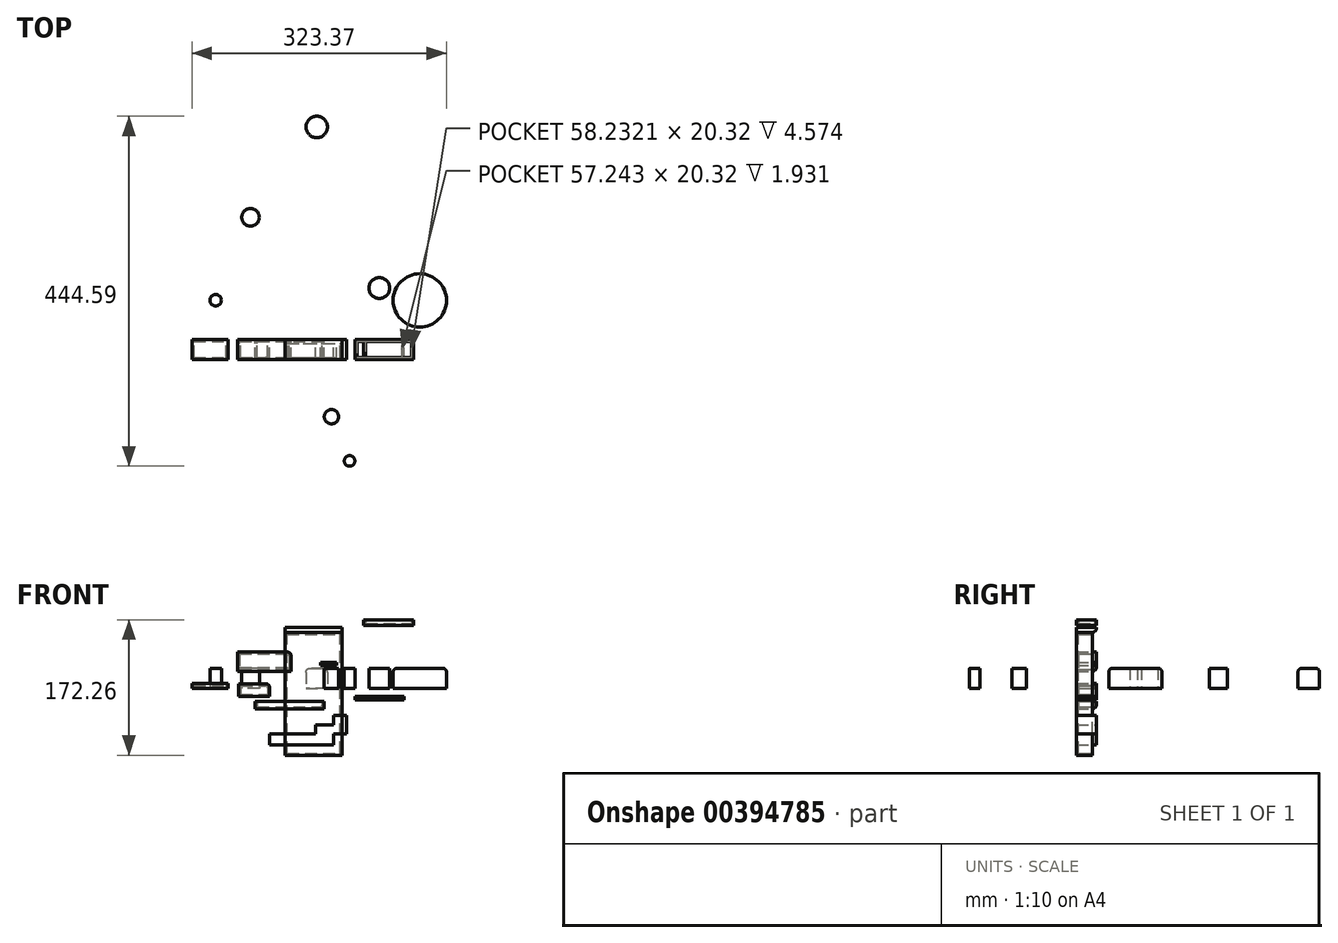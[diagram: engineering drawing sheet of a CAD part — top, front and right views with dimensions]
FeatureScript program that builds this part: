
annotation { "Feature Type Name" : "Feature", "Feature Type Description" : "" }
export const myFeature = defineFeature(function(context is Context, id is Id, definition is map)
    precondition{}
    {
        {
            var Q0;
            Q0=qCreatedBy(makeId("Front.planeOp"),FACE);
            var sketch = newSketch(context, id + "F0", { "sketchPlane" : qUnion([Q0])});
            skLineSegment(sketch, "E0.bottom", {"start": v(-105.2, 46.14) * mm, "end": v(-37.26, 46.14) * mm});
            skLineSegment(sketch, "E0.top", {"start": v(-105.2, 21.56) * mm, "end": v(-37.26, 21.56) * mm});
            skLineSegment(sketch, "E0.left", {"start": v(-105.2, 46.14) * mm, "end": v(-105.2, 21.56) * mm});
            skLineSegment(sketch, "E0.right", {"start": v(-37.26, 46.14) * mm, "end": v(-37.26, 21.56) * mm});
            skLineSegment(sketch, "E1.bottom", {"start": v(-163.23, 6.3) * mm, "end": v(-117.4, 6.3) * mm});
            skLineSegment(sketch, "E1.top", {"start": v(-163.23, 0) * mm, "end": v(-117.4, 0) * mm});
            skLineSegment(sketch, "E1.left", {"start": v(-163.23, 6.3) * mm, "end": v(-163.23, 0) * mm});
            skLineSegment(sketch, "E1.right", {"start": v(-117.4, 6.3) * mm, "end": v(-117.4, 0) * mm});
            skLineSegment(sketch, "E2.bottom", {"start": v(-103.87, 5.63) * mm, "end": v(-64.3, 5.63) * mm});
            skLineSegment(sketch, "E2.top", {"start": v(-103.87, -10.65) * mm, "end": v(-64.3, -10.65) * mm});
            skLineSegment(sketch, "E2.left", {"start": v(-103.87, 5.63) * mm, "end": v(-103.87, -10.65) * mm});
            skLineSegment(sketch, "E2.right", {"start": v(-64.3, 5.63) * mm, "end": v(-64.3, -10.65) * mm});
            skLineSegment(sketch, "E3.bottom", {"start": v(-82.77, -16.97) * mm, "end": v(4.62, -16.97) * mm});
            skLineSegment(sketch, "E3.top", {"start": v(-82.77, -26.04) * mm, "end": v(4.62, -26.04) * mm});
            skLineSegment(sketch, "E3.left", {"start": v(-82.77, -16.97) * mm, "end": v(-82.77, -26.04) * mm});
            skLineSegment(sketch, "E3.right", {"start": v(4.62, -16.97) * mm, "end": v(4.62, -26.04) * mm});
            skLineSegment(sketch, "E4.bottom", {"start": v(0, 32.88) * mm, "end": v(20.77, 32.88) * mm});
            skLineSegment(sketch, "E4.top", {"start": v(0, 29.08) * mm, "end": v(20.77, 29.08) * mm});
            skLineSegment(sketch, "E4.left", {"start": v(0, 32.88) * mm, "end": v(0, 29.08) * mm});
            skLineSegment(sketch, "E4.right", {"start": v(20.77, 32.88) * mm, "end": v(20.77, 29.08) * mm});
            skLineSegment(sketch, "E5.bottom", {"start": v(-44.85, 77.4) * mm, "end": v(27.7, 77.4) * mm});
            skLineSegment(sketch, "E5.top", {"start": v(-44.85, 70.98) * mm, "end": v(27.7, 70.98) * mm});
            skLineSegment(sketch, "E5.left", {"start": v(-44.85, 77.4) * mm, "end": v(-44.85, 70.98) * mm});
            skLineSegment(sketch, "E5.right", {"start": v(27.7, 77.4) * mm, "end": v(27.7, 70.98) * mm});
            skLineSegment(sketch, "E6.bottom", {"start": v(54.74, 87.03) * mm, "end": v(118.05, 87.03) * mm});
            skLineSegment(sketch, "E6.top", {"start": v(54.74, 79.91) * mm, "end": v(118.05, 79.91) * mm});
            skLineSegment(sketch, "E6.left", {"start": v(54.74, 87.03) * mm, "end": v(54.74, 79.91) * mm});
            skLineSegment(sketch, "E6.right", {"start": v(118.05, 87.03) * mm, "end": v(118.05, 79.91) * mm});
            skLineSegment(sketch, "E7.bottom", {"start": v(16.82, -34.39) * mm, "end": v(33.3, -34.39) * mm});
            skLineSegment(sketch, "E7.top", {"start": v(16.82, -57.98) * mm, "end": v(33.3, -57.98) * mm});
            skLineSegment(sketch, "E7.left", {"start": v(16.82, -34.39) * mm, "end": v(16.82, -57.98) * mm});
            skLineSegment(sketch, "E7.right", {"start": v(33.3, -34.39) * mm, "end": v(33.3, -57.98) * mm});
            skLineSegment(sketch, "E8.bottom", {"start": v(-5.94, -46.89) * mm, "end": v(16.82, -46.89) * mm});
            skLineSegment(sketch, "E8.top", {"start": v(-5.94, -57.98) * mm, "end": v(16.82, -57.98) * mm});
            skLineSegment(sketch, "E8.left", {"start": v(-5.94, -46.89) * mm, "end": v(-5.94, -57.98) * mm});
            skLineSegment(sketch, "E8.right", {"start": v(16.82, -46.89) * mm, "end": v(16.82, -57.98) * mm});
            skLineSegment(sketch, "E9.bottom", {"start": v(-64.3, -57.98) * mm, "end": v(16.82, -57.98) * mm});
            skLineSegment(sketch, "E9.top", {"start": v(-64.3, -71.98) * mm, "end": v(16.82, -71.98) * mm});
            skLineSegment(sketch, "E9.left", {"start": v(-64.3, -57.98) * mm, "end": v(-64.3, -71.98) * mm});
            skLineSegment(sketch, "E9.right", {"start": v(16.82, -57.98) * mm, "end": v(16.82, -71.98) * mm});
            skLineSegment(sketch, "E10.bottom", {"start": v(67.6, -72.82) * mm, "end": v(28.36, -72.82) * mm});
            skLineSegment(sketch, "E10.top", {"start": v(67.6, -57.98) * mm, "end": v(28.36, -57.98) * mm});
            skLineSegment(sketch, "E10.left", {"start": v(67.6, -72.82) * mm, "end": v(67.6, -57.98) * mm});
            skLineSegment(sketch, "E10.right", {"start": v(28.36, -72.82) * mm, "end": v(28.36, -57.98) * mm});
            skLineSegment(sketch, "E11.bottom", {"start": v(28.36, -82.82) * mm, "end": v(16.82, -82.82) * mm});
            skLineSegment(sketch, "E11.top", {"start": v(28.36, -57.98) * mm, "end": v(16.82, -57.98) * mm});
            skLineSegment(sketch, "E11.left", {"start": v(28.36, -82.82) * mm, "end": v(28.36, -57.98) * mm});
            skLineSegment(sketch, "E11.right", {"start": v(16.82, -82.82) * mm, "end": v(16.82, -57.98) * mm});
            skLineSegment(sketch, "E12.bottom", {"start": v(28.36, -82.82) * mm, "end": v(67.6, -82.82) * mm});
            skLineSegment(sketch, "E12.top", {"start": v(28.36, -72.82) * mm, "end": v(67.6, -72.82) * mm});
            skLineSegment(sketch, "E12.left", {"start": v(28.36, -82.82) * mm, "end": v(28.36, -72.82) * mm});
            skLineSegment(sketch, "E12.right", {"start": v(67.6, -82.82) * mm, "end": v(67.6, -72.82) * mm});
            skLineSegment(sketch, "E13.bottom", {"start": v(44.19, -14.94) * mm, "end": v(106.5, -14.94) * mm});
            skLineSegment(sketch, "E13.top", {"start": v(44.19, -10.47) * mm, "end": v(106.5, -10.47) * mm});
            skLineSegment(sketch, "E13.left", {"start": v(44.19, -14.94) * mm, "end": v(44.19, -10.47) * mm});
            skLineSegment(sketch, "E13.right", {"start": v(106.5, -14.94) * mm, "end": v(106.5, -10.47) * mm});
            skSolve(sketch);
        }
        {
            var Q0;
            Q0=makeQuery(id+"F0.imprint","IMPRINT",FACE,{"disambiguationData":[TD([[makeQuery(id+"F0.imprint","IMPRINT",EDGE,{"derivedFrom":sQuery(id+"F0.wireOp",EDGE,"E0.bottom")}),-1.0]])]});
            var Q1;
            Q1=makeQuery(id+"F0.imprint","IMPRINT",FACE,{"disambiguationData":[TD([[makeQuery(id+"F0.imprint","IMPRINT",EDGE,{"derivedFrom":sQuery(id+"F0.wireOp",EDGE,"E2.bottom")}),-1.0]])]});
            var Q2;
            Q2=makeQuery(id+"F0.imprint","IMPRINT",FACE,{"disambiguationData":[TD([[makeQuery(id+"F0.imprint","IMPRINT",EDGE,{"derivedFrom":sQuery(id+"F0.wireOp",EDGE,"E1.bottom")}),-1.0]])]});
            var Q3;
            Q3=makeQuery(id+"F0.imprint","IMPRINT",FACE,{"disambiguationData":[TD([[makeQuery(id+"F0.imprint","IMPRINT",EDGE,{"derivedFrom":sQuery(id+"F0.wireOp",EDGE,"E3.bottom")}),-1.0]])]});
            var Q4;
            Q4=makeQuery(id+"F0.imprint","IMPRINT",FACE,{"disambiguationData":[TD([[makeQuery(id+"F0.imprint","IMPRINT",EDGE,{"derivedFrom":sQuery(id+"F0.wireOp",EDGE,"E5.bottom")}),-1.0]])]});
            var Q5;
            Q5=makeQuery(id+"F0.imprint","IMPRINT",FACE,{"disambiguationData":[TD([[makeQuery(id+"F0.imprint","IMPRINT",EDGE,{"derivedFrom":sQuery(id+"F0.wireOp",EDGE,"E4.bottom")}),-1.0]])]});
            var Q6;
            Q6=makeQuery(id+"F0.imprint","IMPRINT",FACE,{"disambiguationData":[TD([[makeQuery(id+"F0.imprint","IMPRINT",EDGE,{"derivedFrom":sQuery(id+"F0.wireOp",EDGE,"E6.bottom")}),-1.0]])]});
            var Q7;
            Q7=makeQuery(id+"F0.imprint","IMPRINT",FACE,{"disambiguationData":[TD([[makeQuery(id+"F0.imprint","IMPRINT",EDGE,{"derivedFrom":sQuery(id+"F0.wireOp",EDGE,"E13.bottom")}),1.0]])]});
            var Q8;
            Q8=makeQuery(id+"F0.imprint","IMPRINT",FACE,{"disambiguationData":[TD([[makeQuery(id+"F0.imprint","IMPRINT",EDGE,{"derivedFrom":sQuery(id+"F0.wireOp",EDGE,"E7.bottom")}),-1.0]])]});
            var Q9;
            Q9=makeQuery(id+"F0.imprint","IMPRINT",FACE,{"disambiguationData":[TD([[makeQuery(id+"F0.imprint","IMPRINT",EDGE,{"derivedFrom":sQuery(id+"F0.wireOp",EDGE,"E8.bottom")}),-1.0]])]});
            var Q10;
            {var subQ1=sQuery(id+"F0.wireOp",EDGE,"E9.top");Q10=makeQuery(id+"F0.imprint","IMPRINT",FACE,{"disambiguationData":[TD([[makeQuery(id+"F0.imprint","IMPRINT",EDGE,{"derivedFrom":subQ1}),1.0]])]});}
            extrude(context, id + "F1", {"entities" : qUnion([Q0, Q1, Q2, Q3, Q4, Q5, Q6, Q7, Q8, Q9, Q10]), "depth" : 25.4 * mm});
        }
        {
            var Q0;
            Q0=makeQuery(id+"F1.opExtrude","SWEPT_EDGE",EDGE,{"disambiguationData":[OSD([sQuery(id+"F0.wireOp",EDGE,"E7.bottom"),sQuery(id+"F0.wireOp",EDGE,"E7.right")])]});
            var Q1;
            Q1=makeQuery(id+"F1.opExtrude","SWEPT_EDGE",EDGE,{"disambiguationData":[OSD([sQuery(id+"F0.wireOp",EDGE,"E0.bottom"),sQuery(id+"F0.wireOp",EDGE,"E0.right")])]});
            var Q2;
            Q2=makeQuery(id+"F1.opExtrude","SWEPT_EDGE",EDGE,{"disambiguationData":[OSD([sQuery(id+"F0.wireOp",EDGE,"E2.bottom"),sQuery(id+"F0.wireOp",EDGE,"E2.right")])]});
            var Q3;
            Q3=makeQuery(id+"F1.opExtrude","SWEPT_EDGE",EDGE,{"disambiguationData":[OSD([sQuery(id+"F0.wireOp",EDGE,"E7.right"),sQuery(id+"F0.wireOp",EDGE,"E10.top")])]});
            var Q4;
            Q4=makeQuery(id+"F1.opExtrude","CAP_EDGE",EDGE,{"disambiguationData":[OSD([sQuery(id+"F0.wireOp",EDGE,"E7.bottom")])],"isStart":false});
            var Q5;
            Q5=makeQuery(id+"F1.opExtrude","SWEPT_EDGE",EDGE,{"disambiguationData":[OSD([sQuery(id+"F0.wireOp",EDGE,"E7.left"),sQuery(id+"F0.wireOp",EDGE,"E8.bottom"),sQuery(id+"F0.wireOp",EDGE,"E8.right")])]});
            var Q6;
            Q6=makeQuery(id+"F1.opExtrude","SWEPT_EDGE",EDGE,{"disambiguationData":[OSD([sQuery(id+"F0.wireOp",EDGE,"E8.bottom"),sQuery(id+"F0.wireOp",EDGE,"E8.left")])]});
            var Q7;
            Q7=makeQuery(id+"F1.opExtrude","SWEPT_EDGE",EDGE,{"disambiguationData":[OSD([sQuery(id+"F0.wireOp",EDGE,"E8.left"),sQuery(id+"F0.wireOp",EDGE,"E9.bottom")])]});
            var Q8;
            Q8=makeQuery(id+"F1.opExtrude","SWEPT_EDGE",EDGE,{"disambiguationData":[OSD([sQuery(id+"F0.wireOp",EDGE,"E7.bottom"),sQuery(id+"F0.wireOp",EDGE,"E7.left")])]});
            var Q9;
            Q9=makeQuery(id+"F1.opExtrude","SWEPT_EDGE",EDGE,{"disambiguationData":[OSD([sQuery(id+"F0.wireOp",EDGE,"E9.bottom"),sQuery(id+"F0.wireOp",EDGE,"E9.left")])]});
            var Q10;
            Q10=makeQuery(id+"F1.opExtrude","SWEPT_EDGE",EDGE,{"disambiguationData":[OSD([sQuery(id+"F0.wireOp",EDGE,"E8.right"),sQuery(id+"F0.wireOp",EDGE,"E9.bottom"),sQuery(id+"F0.wireOp",EDGE,"E11.top"),sQuery(id+"F0.wireOp",EDGE,"E11.right")])]});
            var Q11;
            Q11=makeQuery(id+"F1.opExtrude","SWEPT_FACE",FACE,{"disambiguationData":[OSD([sQuery(id+"F0.wireOp",EDGE,"E9.top")])]});
            var Q12;
            Q12=makeQuery(id+"F1.opExtrude","CAP_EDGE",EDGE,{"disambiguationData":[OSD([sQuery(id+"F0.wireOp",EDGE,"E9.bottom")])],"isStart":true});
            var Q13;
            Q13=makeQuery(id+"F1.opExtrude","CAP_EDGE",EDGE,{"disambiguationData":[OSD([sQuery(id+"F0.wireOp",EDGE,"E10.top"),sQuery(id+"F0.wireOp",EDGE,"E11.top")])],"isStart":true});
            var Q14;
            Q14=makeQuery(id+"F1.opExtrude","CAP_EDGE",EDGE,{"disambiguationData":[OSD([sQuery(id+"F0.wireOp",EDGE,"E7.right")])],"isStart":true});
            var Q15;
            Q15=makeQuery(id+"F1.opExtrude","CAP_EDGE",EDGE,{"disambiguationData":[OSD([sQuery(id+"F0.wireOp",EDGE,"E7.bottom")])],"isStart":true});
            var Q16;
            Q16=makeQuery(id+"F1.opExtrude","CAP_EDGE",EDGE,{"disambiguationData":[OSD([sQuery(id+"F0.wireOp",EDGE,"E8.bottom")])],"isStart":true});
            var Q17;
            Q17=makeQuery(id+"F1.opExtrude","CAP_EDGE",EDGE,{"disambiguationData":[OSD([sQuery(id+"F0.wireOp",EDGE,"E8.bottom")])],"isStart":false});
            var Q18;
            Q18=makeQuery(id+"F1.opExtrude","CAP_EDGE",EDGE,{"disambiguationData":[OSD([sQuery(id+"F0.wireOp",EDGE,"E9.bottom")])],"isStart":false});
            var Q19;
            Q19=makeQuery(id+"F1.opExtrude","CAP_EDGE",EDGE,{"disambiguationData":[OSD([sQuery(id+"F0.wireOp",EDGE,"E9.left")])],"isStart":false});
            var Q20;
            Q20=makeQuery(id+"F1.opExtrude","CAP_EDGE",EDGE,{"disambiguationData":[OSD([sQuery(id+"F0.wireOp",EDGE,"E10.top"),sQuery(id+"F0.wireOp",EDGE,"E11.top")])],"isStart":false});
            var Q21;
            Q21=makeQuery(id+"F1.opExtrude","CAP_EDGE",EDGE,{"disambiguationData":[OSD([sQuery(id+"F0.wireOp",EDGE,"E7.right")])],"isStart":false});
            var Q22;
            Q22=makeQuery(id+"F1.opExtrude","CAP_EDGE",EDGE,{"disambiguationData":[OSD([sQuery(id+"F0.wireOp",EDGE,"E9.left")])],"isStart":true});
            var Q23;
            Q23=makeQuery(id+"F1.opExtrude","CAP_EDGE",EDGE,{"disambiguationData":[OSD([sQuery(id+"F0.wireOp",EDGE,"E3.top")])],"isStart":true});
            var Q24;
            Q24=makeQuery(id+"F1.opExtrude","CAP_EDGE",EDGE,{"disambiguationData":[OSD([sQuery(id+"F0.wireOp",EDGE,"E0.top")])],"isStart":true});
            var Q25;
            Q25=makeQuery(id+"F1.opExtrude","CAP_EDGE",EDGE,{"disambiguationData":[OSD([sQuery(id+"F0.wireOp",EDGE,"E5.top")])],"isStart":true});
            fillet(context, id + "F2", {"entities" : qUnion([Q0, Q1, Q2, Q3, Q4, Q5, Q6, Q7, Q8, Q9, Q10, Q11, Q12, Q13, Q14, Q15, Q16, Q17, Q18, Q19, Q20, Q21, Q22, Q23, Q24, Q25]), "radius" : 5.08 * mm, "tangentPropagation" : true, "allowEdgeOverflow" : false});
        }
        {
            var Q0;
            Q0=makeQuery(id+"F1.opExtrude","SWEPT_FACE",FACE,{"disambiguationData":[OSD([sQuery(id+"F0.wireOp",EDGE,"E5.top")])]});
            extrude(context, id + "F3", {"entities" : qUnion([Q0]), "depth" : 156.2 * mm});
        }
        {
            var Q0;
            Q0=makeQuery(id+"F1.opExtrude","CAP_FACE",FACE,{"disambiguationData":[OSD([sQuery(id+"F0.wireOp",EDGE,"E0.bottom"),sQuery(id+"F0.wireOp",EDGE,"E0.top"),sQuery(id+"F0.wireOp",EDGE,"E0.left"),sQuery(id+"F0.wireOp",EDGE,"E0.right")])],"isStart":true});
            var Q1;
            Q1=makeQuery(id+"F1.opExtrude","CAP_FACE",FACE,{"disambiguationData":[OSD([sQuery(id+"F0.wireOp",EDGE,"E2.bottom"),sQuery(id+"F0.wireOp",EDGE,"E2.top"),sQuery(id+"F0.wireOp",EDGE,"E2.left"),sQuery(id+"F0.wireOp",EDGE,"E2.right")])],"isStart":true});
            var Q2;
            Q2=makeQuery(id+"F1.opExtrude","SWEPT_FACE",FACE,{"disambiguationData":[OSD([sQuery(id+"F0.wireOp",EDGE,"E1.top")])]});
            var Q3;
            Q3=makeQuery(id+"F1.opExtrude","SWEPT_FACE",FACE,{"disambiguationData":[OSD([sQuery(id+"F0.wireOp",EDGE,"E6.bottom")])]});
            var Q4;
            Q4=makeQuery(id+"F1.opExtrude","SWEPT_FACE",FACE,{"disambiguationData":[OSD([sQuery(id+"F0.wireOp",EDGE,"E13.top")])]});
            var Q5;
            {var subQ0=sQuery(id+"F0.wireOp",EDGE,"E5.top");Q5=makeQuery(id+"F3.opExtrude","SWEPT_FACE",FACE,{"disambiguationData":[OSD([subQ0]),TDD([makeQuery(id+"F2.opFillet","BLEND_EDGE",EDGE,{"blendedFrom":[makeQuery(id+"F1.opExtrude","CAP_EDGE",EDGE,{"disambiguationData":[OSD([subQ0])],"isStart":true}),makeQuery(id+"F1.opExtrude","SWEPT_FACE",FACE,{"disambiguationData":[OSD([subQ0])]})],"blendedInto":[makeQuery(id+"F1.opExtrude","SWEPT_FACE",FACE,{"disambiguationData":[OSD([subQ0])]})]})])]});}
            var Q6;
            Q6=makeQuery(id+"F1.opExtrude","SWEPT_FACE",FACE,{"disambiguationData":[OSD([sQuery(id+"F0.wireOp",EDGE,"E3.bottom")])]});
            shell(context, id + "F4", {"entities" : qUnion([Q0, Q1, Q2, Q3, Q4, Q5, Q6]), "thickness" : 2.54 * mm});
        }
        {
            var Q0;
            Q0=qCreatedBy(makeId("Top.planeOp"),FACE);
            var sketch = newSketch(context, id + "F5", { "sketchPlane" : qUnion([Q0])});
            skCircle(sketch, "E14", {"center": v(126.28, 49.46) * mm, "radius": 33.86 * mm});
            skCircle(sketch, "E15", {"center": v(74.8, 65.2) * mm, "radius": 13.22 * mm});
            skCircle(sketch, "E16", {"center": v(-133.1, 49.65) * mm, "radius": 7.3 * mm});
            skCircle(sketch, "E17", {"center": v(-88.77, 155) * mm, "radius": 11.23 * mm});
            skCircle(sketch, "E18", {"center": v(-4.64, 269.77) * mm, "radius": 13.68 * mm});
            skCircle(sketch, "E19", {"center": v(37.05, -154.4) * mm, "radius": 6.76 * mm});
            skCircle(sketch, "E20", {"center": v(14, -98.3) * mm, "radius": 9.12 * mm});
            skSolve(sketch);
        }
        {
            var Q0;
            Q0=makeQuery(id+"F5.imprint","IMPRINT",FACE,{"disambiguationData":[TD([[makeQuery(id+"F5.imprint","IMPRINT",EDGE,{"derivedFrom":sQuery(id+"F5.wireOp",EDGE,"E14")}),1.0]])]});
            var Q1;
            Q1=makeQuery(id+"F5.imprint","IMPRINT",FACE,{"disambiguationData":[TD([[makeQuery(id+"F5.imprint","IMPRINT",EDGE,{"derivedFrom":sQuery(id+"F5.wireOp",EDGE,"E15")}),1.0]])]});
            var Q2;
            Q2=makeQuery(id+"F5.imprint","IMPRINT",FACE,{"disambiguationData":[TD([[makeQuery(id+"F5.imprint","IMPRINT",EDGE,{"derivedFrom":sQuery(id+"F5.wireOp",EDGE,"E19")}),1.0]])]});
            var Q3;
            Q3=makeQuery(id+"F5.imprint","IMPRINT",FACE,{"disambiguationData":[TD([[makeQuery(id+"F5.imprint","IMPRINT",EDGE,{"derivedFrom":sQuery(id+"F5.wireOp",EDGE,"E20")}),1.0]])]});
            var Q4;
            Q4=makeQuery(id+"F5.imprint","IMPRINT",FACE,{"disambiguationData":[TD([[makeQuery(id+"F5.imprint","IMPRINT",EDGE,{"derivedFrom":sQuery(id+"F5.wireOp",EDGE,"E18")}),1.0]])]});
            var Q5;
            Q5=makeQuery(id+"F5.imprint","IMPRINT",FACE,{"disambiguationData":[TD([[makeQuery(id+"F5.imprint","IMPRINT",EDGE,{"derivedFrom":sQuery(id+"F5.wireOp",EDGE,"E17")}),1.0]])]});
            var Q6;
            Q6=makeQuery(id+"F5.imprint","IMPRINT",FACE,{"disambiguationData":[TD([[makeQuery(id+"F5.imprint","IMPRINT",EDGE,{"derivedFrom":sQuery(id+"F5.wireOp",EDGE,"E16")}),1.0]])]});
            extrude(context, id + "F6", {"entities" : qUnion([Q0, Q1, Q2, Q3, Q4, Q5, Q6]), "depth" : 25.4 * mm});
        }
        {
            var Q0;
            Q0=qCreatedBy(makeId("Right.planeOp"),FACE);
            var sketch = newSketch(context, id + "F7", { "sketchPlane" : qUnion([Q0])});
            skFitSpline(sketch, "E21", {"points": [v(31.35, 10.9) * mm, v(72.94, 55.5) * mm, v(201.32, 110.3) * mm, v(270.57, 165.22) * mm, v(169.43, 138.99) * mm, v(28.61, 53.37) * mm], "startDerivative": vector(217.23, 320.06) * mm, "endDerivative": vector(-519.54, -373.27) * mm});
            skSolve(sketch);
        }
        {
            var Q0;
            Q0=makeQuery(id+"F6.opExtrude","CAP_EDGE",EDGE,{"disambiguationData":[OSD([sQuery(id+"F5.wireOp",EDGE,"E14")])],"isStart":false});
            var Q1;
            Q1=makeQuery(id+"F6.opExtrude","CAP_EDGE",EDGE,{"disambiguationData":[OSD([sQuery(id+"F5.wireOp",EDGE,"E18")])],"isStart":false});
            fillet(context, id + "F8", {"entities" : qUnion([Q0, Q1]), "radius" : 5.08 * mm, "tangentPropagation" : true, "allowEdgeOverflow" : false});
        }
    });
